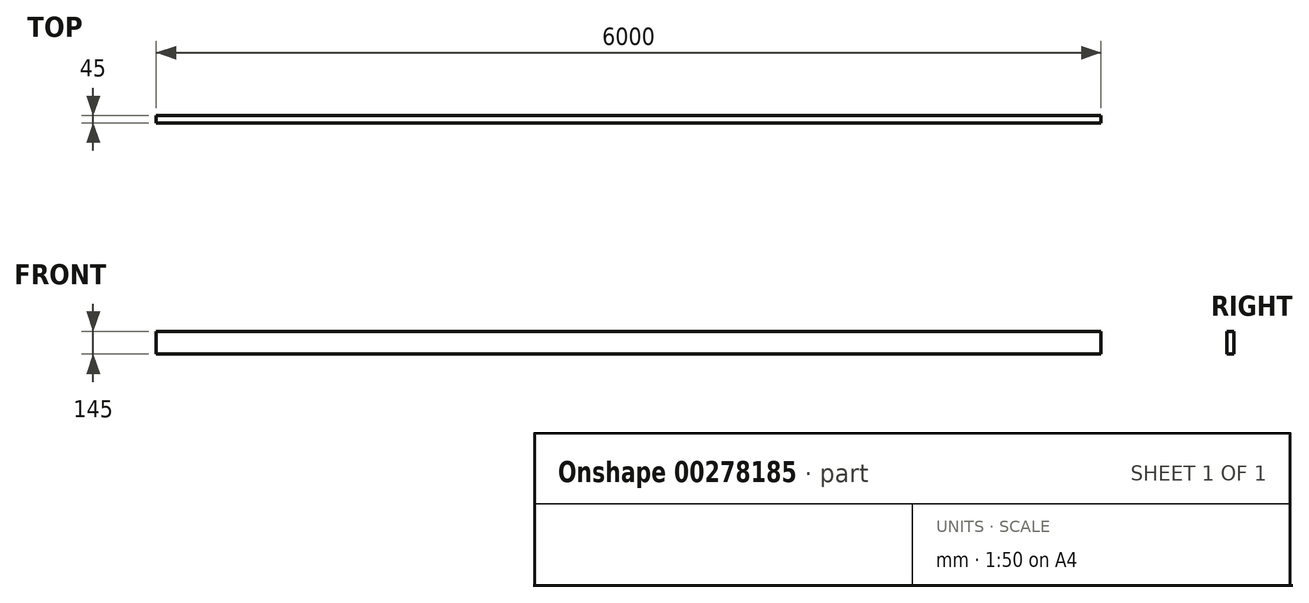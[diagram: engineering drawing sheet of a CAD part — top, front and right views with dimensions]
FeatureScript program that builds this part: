
annotation { "Feature Type Name" : "Feature", "Feature Type Description" : "" }
export const myFeature = defineFeature(function(context is Context, id is Id, definition is map)
    precondition{}
    {
        {
            var Q0;
            Q0=qCreatedBy(makeId("Right.planeOp"),FACE);
            var sketch = newSketch(context, id + "F0", { "sketchPlane" : qUnion([Q0])});
            skLineSegment(sketch, "E0.bottom", {"start": v(-45, 145) * mm, "end": v(0, 145) * mm});
            skLineSegment(sketch, "E0.top", {"start": v(-45, 0) * mm, "end": v(0, 0) * mm});
            skLineSegment(sketch, "E0.left", {"start": v(-45, 145) * mm, "end": v(-45, 0) * mm});
            skLineSegment(sketch, "E0.right", {"start": v(0, 145) * mm, "end": v(0, 0) * mm});
            skSolve(sketch);
        }
        {
            var Q0;
            Q0 = qSketchRegion(id + "F0", true);
            extrude(context, id + "F1", {"entities" : qUnion([Q0]), "depth" : 6000 * mm});
        }
    });
